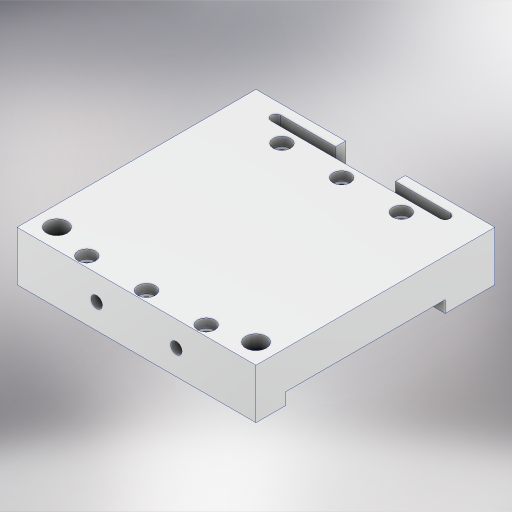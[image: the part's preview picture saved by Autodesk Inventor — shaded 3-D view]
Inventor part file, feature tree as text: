
AUTODESK INVENTOR PART (.ipt)
format: ipt  version: 2024 (Build 280153000, 153)  size: 478,720 bytes
history: native  units: in
note: dims shown in document units (in); Inventor stores cm internally (conversion verified against a paired STEP export)
features: hole x7, extrude x4, sketch x1
ambient origin geometry x8: Origin, YZ Plane, XZ Plane, XY Plane, X Axis, Y Axis, Z Axis, Center Point
bodies: Solid1 (feature_tree)
feature tree (12):
  extrude  "Extrusion1"  Depth=0.112in
  extrude  "Extrusion2"  Depth=0.625in TaperAngle=0.0deg
  hole  "Hole1"  [1 undecoded]
  hole  "Hole2"  [1 undecoded]
  extrude  "Extrusion4"  Depth=0.112in
  hole  "Hole4"  [1 undecoded]
  hole  "Hole5"  [1 undecoded]
  hole  "Hole6"  [1 undecoded]
  extrude  "Extrusion5"  Depth=0.112in
  hole  "Hole7"  [1 undecoded]
  hole  "Hole8"  [1 undecoded]
  sketch  "Sketch13"  dims[d0=3.0in d1=3.0in d2=0.625in d3=0.0in d4=0.75in d5=0.25in d6=0.125in d7=0.75in d8=0.0in d9=0.0in d10=0.75in d11=0.125in d12=0.125in d13=0.125in d14=0.0561in d15=0.146in d16=0.375in d17=0.25in d18=0.5635in d19=0.375in d20=0.8108in d21=0.25in d22=0.25in d23=0.081in d24=0.146in d25=0.146in d26=0.25in d27=0.5635in d28=0.375in d29=0.8108in d32=0.25in d33=2.0in d34=0.375in d35=0.25in d36=2.0in d37=0.375in d38=0.15in d39=0.0in d51=0.0625in d52=0.625in d53=0.3125in d54=0.8in d55=0.234in d56=0.2711in d57=0.0246in d58=0.2346in d59=0.375in d60=0.25in d61=0.5635in d62=2.0in d63=0.8108in d64=1.0in d65=3.0in d66=2.0in d67=0.625in d68=0.3125in d69=0.145in d70=0.38in d71=0.0246in d72=0.2346in d73=0.375in d74=0.25in d75=0.5635in d76=2.15in d77=0.8108in d78=1.0in d79=1.0in d80=0.625in d81=2.0in d82=0.096in d83=0.271in d84=0.375in d85=0.25in d86=0.5635in d87=0.25in d88=0.8108in d89=0.05in d90=0.05in d91=0.0156in d92=0.0in d93=0.25in d94=0.25in d95=0.25in d96=0.26in d97=0.75in d98=0.375in d99=0.25in d100=0.5635in d101=1.0in d102=0.8108in d103=0.125in d104=0.75in d105=0.75in d106=0.425in d107=0.75in d108=0.75in d109=0.129in d110=0.75in d111=0.219in d112=0.112in d113=0.5635in d114=1.0in d115=0.8108in d116=0.0625in d117=0.0625in d118=0.0625in d119=0.0625in]
note: 7 required parameter values undecoded (feature->parameter linkage not recoverable at this tier; creation-order binding heuristic only, values carry confidence <= 0.55)
